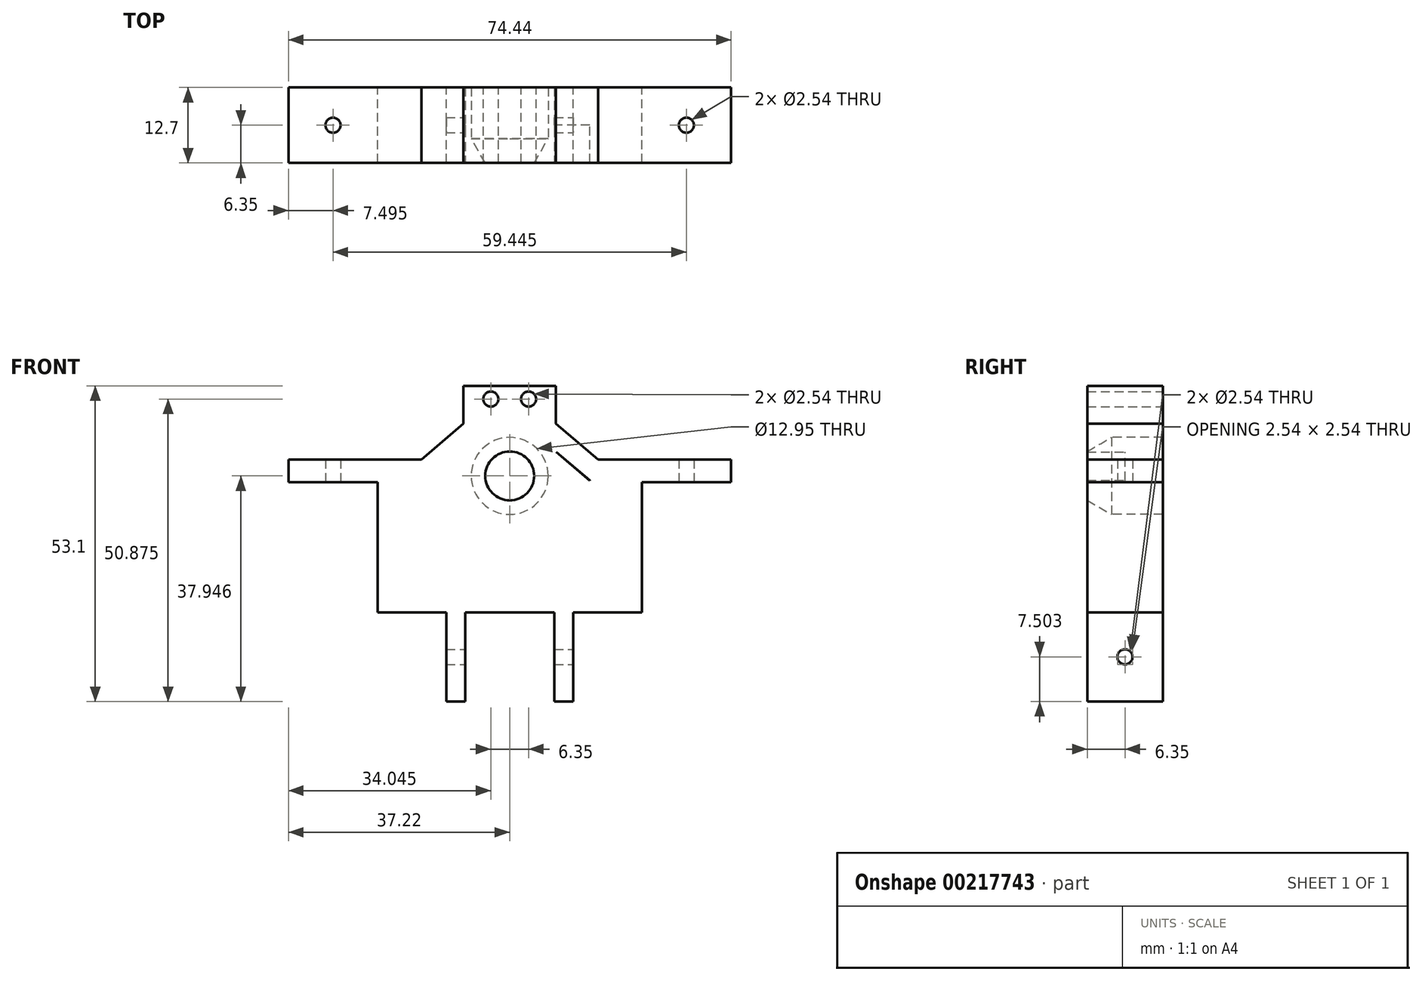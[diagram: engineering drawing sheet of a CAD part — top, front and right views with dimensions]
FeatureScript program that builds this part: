
annotation { "Feature Type Name" : "Feature", "Feature Type Description" : "" }
export const myFeature = defineFeature(function(context is Context, id is Id, definition is map)
    precondition{}
    {
        {
            var Q0;
            Q0=qCreatedBy(makeId("Front.planeOp"),FACE);
            var sketch = newSketch(context, id + "F0", { "sketchPlane" : qUnion([Q0])});
            skLineSegment(sketch, "E0", {"start": v(0, 0.13) * mm, "end": v(7.5, 0.13) * mm});
            skLineSegment(sketch, "E1", {"start": v(-22.22, 19.5) * mm, "end": v(-22.22, 4.52) * mm});
            skLineSegment(sketch, "E2", {"start": v(-7.5, 0.13) * mm, "end": v(0, 0.13) * mm});
            skArc(sketch, "E3", {"start": v(-13.47, 22.3) * mm, "mid": v(-14.04, 9.06) * mm, "end": v(-1.65, 13.77) * mm});
            skArc(sketch, "E4.MirrorC", {"start": v(13.47, 22.3) * mm, "mid": v(14.05, 9.06) * mm, "end": v(1.65, 13.75) * mm});
            skArc(sketch, "E5", {"start": v(1.65, 13.75) * mm, "mid": v(0, 14.71) * mm, "end": v(-1.65, 13.77) * mm});
            skLineSegment(sketch, "E6", {"start": v(-22.22, 19.5) * mm, "end": v(-22.22, 0.13) * mm});
            skLineSegment(sketch, "E7.MirrorCS", {"start": v(22.22, 19.5) * mm, "end": v(22.22, 0.13) * mm});
            skLineSegment(sketch, "E8", {"start": v(0, 0.13) * mm, "end": v(-22.22, 0.13) * mm});
            skLineSegment(sketch, "E9", {"start": v(0, 0.13) * mm, "end": v(22.22, 0.13) * mm});
            skPoint(sketch, "E10.orphan", {"position": v(-22.22, 0) * mm});
            skLineSegment(sketch, "E11", {"start": v(-3.18, 27.12) * mm, "end": v(-3.18, 30.3) * mm});
            skLineSegment(sketch, "E12", {"start": v(3.17, 30.3) * mm, "end": v(3.17, 27.12) * mm});
            skLineSegment(sketch, "E13", {"start": v(3.17, 27.12) * mm, "end": v(3.17, 27.12) * mm});
            skLineSegment(sketch, "E14", {"start": v(-22.22, 19.5) * mm, "end": v(-7.77, 31.88) * mm});
            skLineSegment(sketch, "E15", {"start": v(-3.18, 27.12) * mm, "end": v(-7.84, 27.12) * mm});
            skLineSegment(sketch, "E16", {"start": v(-13.47, 22.3) * mm, "end": v(-7.84, 27.12) * mm});
            skLineSegment(sketch, "E17.MirrorCS", {"start": v(3.17, 27.12) * mm, "end": v(7.84, 27.12) * mm});
            skLineSegment(sketch, "E18.MirrorCS", {"start": v(13.46, 22.3) * mm, "end": v(7.84, 27.12) * mm});
            skLineSegment(sketch, "E19.MirrorCS", {"start": v(3.17, 30.3) * mm, "end": v(3.18, 30.3) * mm});
            skLineSegment(sketch, "E20.MirrorCS", {"start": v(22.22, 19.5) * mm, "end": v(7.77, 31.88) * mm});
            skPoint(sketch, "E21.end.orphan", {"position": v(-9.63, 30.3) * mm});
            skPoint(sketch, "E22.orphan", {"position": v(9.62, 30.3) * mm});
            skPoint(sketch, "E23.start.orphan", {"position": v(0, 27.12) * mm});
            skLineSegment(sketch, "E24", {"start": v(13.47, 22.3) * mm, "end": v(7.84, 27.12) * mm});
            skLineSegment(sketch, "E25", {"start": v(3.17, 27.12) * mm, "end": v(3.17, 30.3) * mm});
            skLineSegment(sketch, "E26", {"start": v(-3.18, 30.3) * mm, "end": v(-3.18, 27.12) * mm});
            skLineSegment(sketch, "E27", {"start": v(-7.84, 27.12) * mm, "end": v(-13.47, 22.3) * mm});
            skArc(sketch, "E28", {"start": v(1.65, 13.75) * mm, "mid": v(14.06, 9.07) * mm, "end": v(13.45, 22.31) * mm});
            skPoint(sketch, "E29.startSnap0", {"position": v(0, 30.3) * mm});
            skPoint(sketch, "E30.orphan", {"position": v(22.22, 2.54) * mm});
            skLineSegment(sketch, "E31", {"start": v(3.17, 30.3) * mm, "end": v(3.17, 33.47) * mm});
            skLineSegment(sketch, "E32", {"start": v(3.17, 33.47) * mm, "end": v(-3.18, 33.47) * mm});
            skLineSegment(sketch, "E33", {"start": v(-3.18, 33.47) * mm, "end": v(-3.18, 30.3) * mm});
            skLineSegment(sketch, "E34", {"start": v(-7.77, 31.88) * mm, "end": v(-7.77, 38.23) * mm});
            skLineSegment(sketch, "E35", {"start": v(7.77, 31.88) * mm, "end": v(7.77, 38.23) * mm});
            skLineSegment(sketch, "E36", {"start": v(7.77, 38.23) * mm, "end": v(-7.77, 38.23) * mm});
            skCircle(sketch, "E37", {"center": v(-9.4, 15.5) * mm, "radius": 7.94 * mm});
            skCircle(sketch, "E38", {"center": v(9.4, 15.5) * mm, "radius": 7.94 * mm});
            skCircle(sketch, "E39", {"center": v(0, 23.08) * mm, "radius": 3.97 * mm});
            skLineSegment(sketch, "E40", {"start": v(-22.22, 0.13) * mm, "end": v(-22.22, 25.81) * mm});
            skLineSegment(sketch, "E41", {"start": v(-22.22, 25.81) * mm, "end": v(-17.42, 25.81) * mm});
            skLineSegment(sketch, "E42", {"start": v(-17.42, 25.81) * mm, "end": v(-12.1, 25.81) * mm});
            skLineSegment(sketch, "E43", {"start": v(0, 12.81) * mm, "end": v(0, 7.67) * mm});
            skLineSegment(sketch, "E44.MirrorCS", {"start": v(22.22, 0.13) * mm, "end": v(22.22, 25.81) * mm});
            skLineSegment(sketch, "E45.MirrorCS", {"start": v(22.22, 25.81) * mm, "end": v(17.42, 25.81) * mm});
            skLineSegment(sketch, "E46.MirrorCS", {"start": v(17.42, 25.81) * mm, "end": v(12.09, 25.81) * mm});
            skCircle(sketch, "E47", {"center": v(3.17, 36) * mm, "radius": 1.27 * mm});
            skCircle(sketch, "E48", {"center": v(-3.18, 36) * mm, "radius": 1.27 * mm});
            skSolve(sketch);
        }
        {
            var Q0;
            Q0=qSketchRegion(id+"F0",true);
            var Q1;
            {var subQ0=sQuery(id+"F0.wireOp",EDGE,"E38");var subQ1=makeQuery(id+"F0.imprint","INTERSECT",VERTEX,{"derivedFrom":[sQuery(id+"F0.wireOp",EDGE,"E24"),subQ0]});Q1=makeQuery(id+"F0.imprint","IMPRINT",FACE,{"disambiguationData":[TD([[makeQuery(id+"F0.imprint","IMPRINT",EDGE,{"disambiguationData":[TD([[subQ1,-1.0]])],"derivedFrom":subQ0}),1.0]])]});}
            var Q2;
            {var subQ0=sQuery(id+"F0.wireOp",EDGE,"E37");var subQ1=makeQuery(id+"F0.imprint","INTERSECT",VERTEX,{"derivedFrom":[sQuery(id+"F0.wireOp",EDGE,"E27"),subQ0]});Q2=makeQuery(id+"F0.imprint","IMPRINT",FACE,{"disambiguationData":[TD([[makeQuery(id+"F0.imprint","IMPRINT",EDGE,{"disambiguationData":[TD([[subQ1,-1.0]])],"derivedFrom":subQ0}),1.0]])]});}
            var Q3;
            Q3=makeQuery(id+"F0.imprint","IMPRINT",FACE,{"disambiguationData":[TD([[makeQuery(id+"F0.imprint","IMPRINT",EDGE,{"derivedFrom":sQuery(id+"F0.wireOp",EDGE,"E15")}),1.0]])]});
            extrude(context, id + "F1", {"entities" : qUnion([Q0, Q1, Q2, Q3]), "depth" : 6.35 * mm});
        }
        {
            var Q0;
            Q0=makeQuery(id+"F1.opExtrude","CAP_FACE",FACE,{"disambiguationData":[OSD([sQuery(id+"F0.wireOp",EDGE,"E6"),sQuery(id+"F0.wireOp",EDGE,"E7.MirrorCS"),sQuery(id+"F0.wireOp",EDGE,"E8"),sQuery(id+"F0.wireOp",EDGE,"E9"),sQuery(id+"F0.wireOp",EDGE,"E14"),sQuery(id+"F0.wireOp",EDGE,"E18.MirrorCS"),sQuery(id+"F0.wireOp",EDGE,"E20.MirrorCS"),sQuery(id+"F0.wireOp",EDGE,"E24"),sQuery(id+"F0.wireOp",EDGE,"E34"),sQuery(id+"F0.wireOp",EDGE,"E35"),sQuery(id+"F0.wireOp",EDGE,"E36"),sQuery(id+"F0.wireOp",EDGE,"E38"),sQuery(id+"F0.wireOp",EDGE,"E39")])],"isStart":true});
            var sketch = newSketch(context, id + "F2", { "sketchPlane" : qUnion([Q0])});
            skCircle(sketch, "E49", {"center": v(0, 23.08) * mm, "radius": 6.48 * mm});
            skLineSegment(sketch, "E50", {"start": v(-22.22, 0.13) * mm, "end": v(22.22, 0.13) * mm});
            skLineSegment(sketch, "E51", {"start": v(7.77, 31.88) * mm, "end": v(7.77, 31.88) * mm});
            skLineSegment(sketch, "E52", {"start": v(7.77, 31.88) * mm, "end": v(7.77, 38.23) * mm});
            skLineSegment(sketch, "E53", {"start": v(7.77, 38.23) * mm, "end": v(-7.77, 38.23) * mm});
            skLineSegment(sketch, "E54", {"start": v(-7.77, 38.23) * mm, "end": v(-7.77, 31.88) * mm});
            skLineSegment(sketch, "E55", {"start": v(-7.77, 31.88) * mm, "end": v(-7.77, 31.88) * mm});
            skLineSegment(sketch, "E56", {"start": v(22.22, 0.13) * mm, "end": v(22.22, 25.81) * mm});
            skLineSegment(sketch, "E57", {"start": v(-22.22, 0.13) * mm, "end": v(-22.22, 25.81) * mm});
            skLineSegment(sketch, "E58", {"start": v(-22.22, 25.81) * mm, "end": v(-14.86, 25.81) * mm});
            skLineSegment(sketch, "E59", {"start": v(-14.86, 25.81) * mm, "end": v(-7.77, 31.88) * mm});
            skLineSegment(sketch, "E60", {"start": v(22.22, 25.81) * mm, "end": v(14.86, 25.81) * mm});
            skLineSegment(sketch, "E61", {"start": v(14.86, 25.81) * mm, "end": v(7.77, 31.88) * mm});
            skCircle(sketch, "E62", {"center": v(-3.17, 36) * mm, "radius": 1.27 * mm});
            skCircle(sketch, "E63", {"center": v(3.18, 36) * mm, "radius": 1.27 * mm});
            skSolve(sketch);
        }
        {
            var Q0;
            Q0 = qSketchRegion(id + "F2", true);
            extrude(context, id + "F3", {"entities" : qUnion([Q0]), "operationType" : NewBodyOperationType.ADD, "depth" : 6.35 * mm});
        }
        {
            var Q0;
            Q0=makeQuery(id+"F1.opExtrude","CAP_EDGE",EDGE,{"disambiguationData":[OSD([sQuery(id+"F0.wireOp",EDGE,"E39")])],"isStart":true});
            chamfer(context, id + "F4", {"entities" : qUnion([Q0]), "chamferType" : ChamferType.OFFSET_ANGLE, "width" : 3.8 * mm, "oppositeDirection" : false, "angle" : 60 * degree, "tangentPropagation" : true});
        }
        {
            var Q0;
            Q0=makeQuery(id+"F3.boolean.opBoolean","MERGE",FACE,{"derivedFrom":[makeQuery(id+"F1.opExtrude","SWEPT_FACE",FACE,{"disambiguationData":[OSD([sQuery(id+"F0.wireOp",EDGE,"E40")])]}),makeQuery(id+"F3.opExtrude","SWEPT_FACE",FACE,{"disambiguationData":[OSD([sQuery(id+"F2.wireOp",EDGE,"E56")])]})]});
            var sketch = newSketch(context, id + "F5", { "sketchPlane" : qUnion([Q0])});
            skLineSegment(sketch, "E64", {"start": v(6.35, 0.13) * mm, "end": v(6.35, 22) * mm});
            skLineSegment(sketch, "E65", {"start": v(6.35, 22) * mm, "end": v(-6.35, 22) * mm});
            skLineSegment(sketch, "E66", {"start": v(-6.35, 22) * mm, "end": v(-6.35, 25.81) * mm});
            skLineSegment(sketch, "E67", {"start": v(-6.35, 25.81) * mm, "end": v(6.35, 25.81) * mm});
            skLineSegment(sketch, "E68", {"start": v(6.35, 25.81) * mm, "end": v(6.35, 22) * mm});
            skSolve(sketch);
        }
        {
            var Q0;
            Q0 = qSketchRegion(id + "F5", true);
            extrude(context, id + "F6", {"entities" : qUnion([Q0]), "operationType" : NewBodyOperationType.ADD, "depth" : 15 * mm});
        }
        {
            var Q0;
            Q0=makeQuery(id+"F6.opExtrude","SWEPT_FACE",FACE,{"disambiguationData":[OSD([sQuery(id+"F5.wireOp",EDGE,"E65")])]});
            var sketch = newSketch(context, id + "F7", { "sketchPlane" : qUnion([Q0])});
            skLineSegment(sketch, "E69", {"start": v(-37.22, -6.35) * mm, "end": v(-22.22, 6.35) * mm});
            skCircle(sketch, "E70", {"center": v(-29.72, 0) * mm, "radius": 1.27 * mm});
            skSolve(sketch);
        }
        {
            var Q0;
            Q0 = qSketchRegion(id + "F7", true);
            extrude(context, id + "F8", {"entities" : qUnion([Q0]), "operationType" : NewBodyOperationType.REMOVE, "oppositeDirection" : true, "depth" : 25.4 * mm});
        }
        {
            var Q0;
            Q0=makeQuery(id+"F3.boolean.opBoolean","MERGE",FACE,{"derivedFrom":[makeQuery(id+"F1.opExtrude","SWEPT_FACE",FACE,{"disambiguationData":[OSD([sQuery(id+"F0.wireOp",EDGE,"E44.MirrorCS")])]}),makeQuery(id+"F3.opExtrude","SWEPT_FACE",FACE,{"disambiguationData":[OSD([sQuery(id+"F2.wireOp",EDGE,"E57")])]})]});
            var sketch = newSketch(context, id + "F9", { "sketchPlane" : qUnion([Q0])});
            skLineSegment(sketch, "E71", {"start": v(-6.35, 0.13) * mm, "end": v(-6.35, 25.81) * mm});
            skLineSegment(sketch, "E72", {"start": v(-6.35, 25.81) * mm, "end": v(6.35, 25.81) * mm});
            skLineSegment(sketch, "E73", {"start": v(6.35, 25.81) * mm, "end": v(6.35, 22) * mm});
            skLineSegment(sketch, "E74", {"start": v(6.35, 22) * mm, "end": v(-6.35, 22) * mm});
            skSolve(sketch);
        }
        {
            var Q0;
            Q0 = qSketchRegion(id + "F9", true);
            extrude(context, id + "F10", {"entities" : qUnion([Q0]), "operationType" : NewBodyOperationType.ADD, "depth" : 15 * mm});
        }
        {
            var Q0;
            Q0=makeQuery(id+"F10.opExtrude","SWEPT_FACE",FACE,{"disambiguationData":[OSD([sQuery(id+"F9.wireOp",EDGE,"E74")])]});
            var sketch = newSketch(context, id + "F11", { "sketchPlane" : qUnion([Q0])});
            skLineSegment(sketch, "E75", {"start": v(37.22, 6.35) * mm, "end": v(22.22, -6.35) * mm});
            skCircle(sketch, "E76", {"center": v(29.72, 0) * mm, "radius": 1.27 * mm});
            skSolve(sketch);
        }
        {
            var Q0;
            Q0 = qSketchRegion(id + "F11", true);
            extrude(context, id + "F12", {"entities" : qUnion([Q0]), "operationType" : NewBodyOperationType.REMOVE, "oppositeDirection" : true, "depth" : 25.4 * mm});
        }
        {
            var Q0;
            Q0=makeQuery(id+"F3.boolean.opBoolean","MERGE",FACE,{"derivedFrom":[makeQuery(id+"F1.opExtrude","SWEPT_FACE",FACE,{"disambiguationData":[OSD([sQuery(id+"F0.wireOp",EDGE,"E8"),sQuery(id+"F0.wireOp",EDGE,"E9")])]}),makeQuery(id+"F3.opExtrude","SWEPT_FACE",FACE,{"disambiguationData":[OSD([sQuery(id+"F2.wireOp",EDGE,"E50")])]})]});
            var sketch = newSketch(context, id + "F13", { "sketchPlane" : qUnion([Q0])});
            skLineSegment(sketch, "E77", {"start": v(0, -6.35) * mm, "end": v(7.5, -6.35) * mm});
            skLineSegment(sketch, "E78", {"start": v(0, -6.35) * mm, "end": v(-7.5, -6.35) * mm});
            skLineSegment(sketch, "E79", {"start": v(-7.5, -6.35) * mm, "end": v(-7.5, 6.35) * mm});
            skLineSegment(sketch, "E80", {"start": v(-7.5, 6.35) * mm, "end": v(-10.67, 6.35) * mm});
            skLineSegment(sketch, "E81", {"start": v(-10.67, 6.35) * mm, "end": v(-10.67, -6.35) * mm});
            skLineSegment(sketch, "E82", {"start": v(-10.67, -6.35) * mm, "end": v(-7.5, -6.35) * mm});
            skLineSegment(sketch, "E83", {"start": v(7.5, -6.35) * mm, "end": v(7.5, 6.35) * mm});
            skLineSegment(sketch, "E84", {"start": v(7.5, 6.35) * mm, "end": v(10.67, 6.35) * mm});
            skLineSegment(sketch, "E85", {"start": v(10.67, 6.35) * mm, "end": v(10.67, -6.35) * mm});
            skLineSegment(sketch, "E86", {"start": v(10.67, -6.35) * mm, "end": v(7.5, -6.35) * mm});
            skSolve(sketch);
        }
        {
            var Q0;
            Q0 = qSketchRegion(id + "F13", true);
            extrude(context, id + "F14", {"entities" : qUnion([Q0]), "operationType" : NewBodyOperationType.ADD, "depth" : 15 * mm});
        }
        {
            var Q0;
            Q0=makeQuery(id+"F14.opExtrude","SWEPT_FACE",FACE,{"disambiguationData":[OSD([sQuery(id+"F13.wireOp",EDGE,"E85")])]});
            var sketch = newSketch(context, id + "F15", { "sketchPlane" : qUnion([Q0])});
            skLineSegment(sketch, "E87", {"start": v(-6.35, 0.13) * mm, "end": v(6.35, -14.87) * mm});
            skCircle(sketch, "E88", {"center": v(0, -7.37) * mm, "radius": 1.27 * mm});
            skSolve(sketch);
        }
        {
            var Q0;
            Q0 = qSketchRegion(id + "F15", true);
            extrude(context, id + "F16", {"entities" : qUnion([Q0]), "operationType" : NewBodyOperationType.REMOVE, "oppositeDirection" : true, "depth" : 25.4 * mm});
        }
    });
